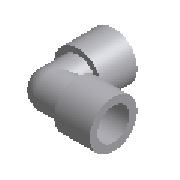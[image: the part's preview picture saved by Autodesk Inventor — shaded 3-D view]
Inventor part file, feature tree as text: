
AUTODESK INVENTOR PART (.ipt)
format: ipt  version: 2023 (Build 270158000, 158)  size: 241,664 bytes
history: native  units: mm (DEFAULTED — no unit token found)
features: sketch x6, extrude x6, other x6, plane x2, fillet x1
ambient origin geometry x8: Origin, YZ Plane, XZ Plane, XY Plane, X Axis, Y Axis, Z Axis, Center Point
bodies: Solid1 (feature_tree)
feature tree (21):
  sketch  "Sketch1"  dims[d0=41.2mm d1=52.4mm]
  plane  "Work Plane1"
  extrude  "Extrusion1"  Depth=52.4mm
  plane  "Work Plane2"
  extrude  "Extrusion2"  TaperAngle=0.0deg  [1 undecoded]
  extrude  "Extrusion3"  Depth=44.5mm
  extrude  "Extrusion4"  Depth=52.4mm
  extrude  "Extrusion5"  TaperAngle=0.0deg  [1 undecoded]
  extrude  "Extrusion6"  Depth=44.5mm
  fillet  "Fillet1"  [1 undecoded]
  other  "Work Axis1"
  other  "Work Point1"
  other  "Work Point2"
  other  "Work Axis2"
  other  "Work Point3"
  other  "Work Point4"
  sketch  "Sketch3"  dims[d49=70.7mm d2=0.0mm]
  sketch  "Sketch4"  dims[d3=44.5mm d4=44.5mm]
  sketch  "Sketch5"  dims[d5=41.2mm d6=52.4mm]
  sketch  "Sketch6"  dims[d55=70.7mm d7=0.0mm]
  sketch  "Sketch7"  dims[d8=44.5mm d9=44.5mm d10=90.0deg d11=60.3mm d12=18.3mm d13=0.0mm d14=60.3mm d15=18.3mm d16=0.0mm d17=49.1mm d18=12.7mm d19=0.0mm d20=49.1mm d21=12.7mm d22=0.0mm d23=15.0mm d24=20.6mm]
note: 3 required parameter values undecoded (feature->parameter linkage not recoverable at this tier; creation-order binding heuristic only, values carry confidence <= 0.55)
